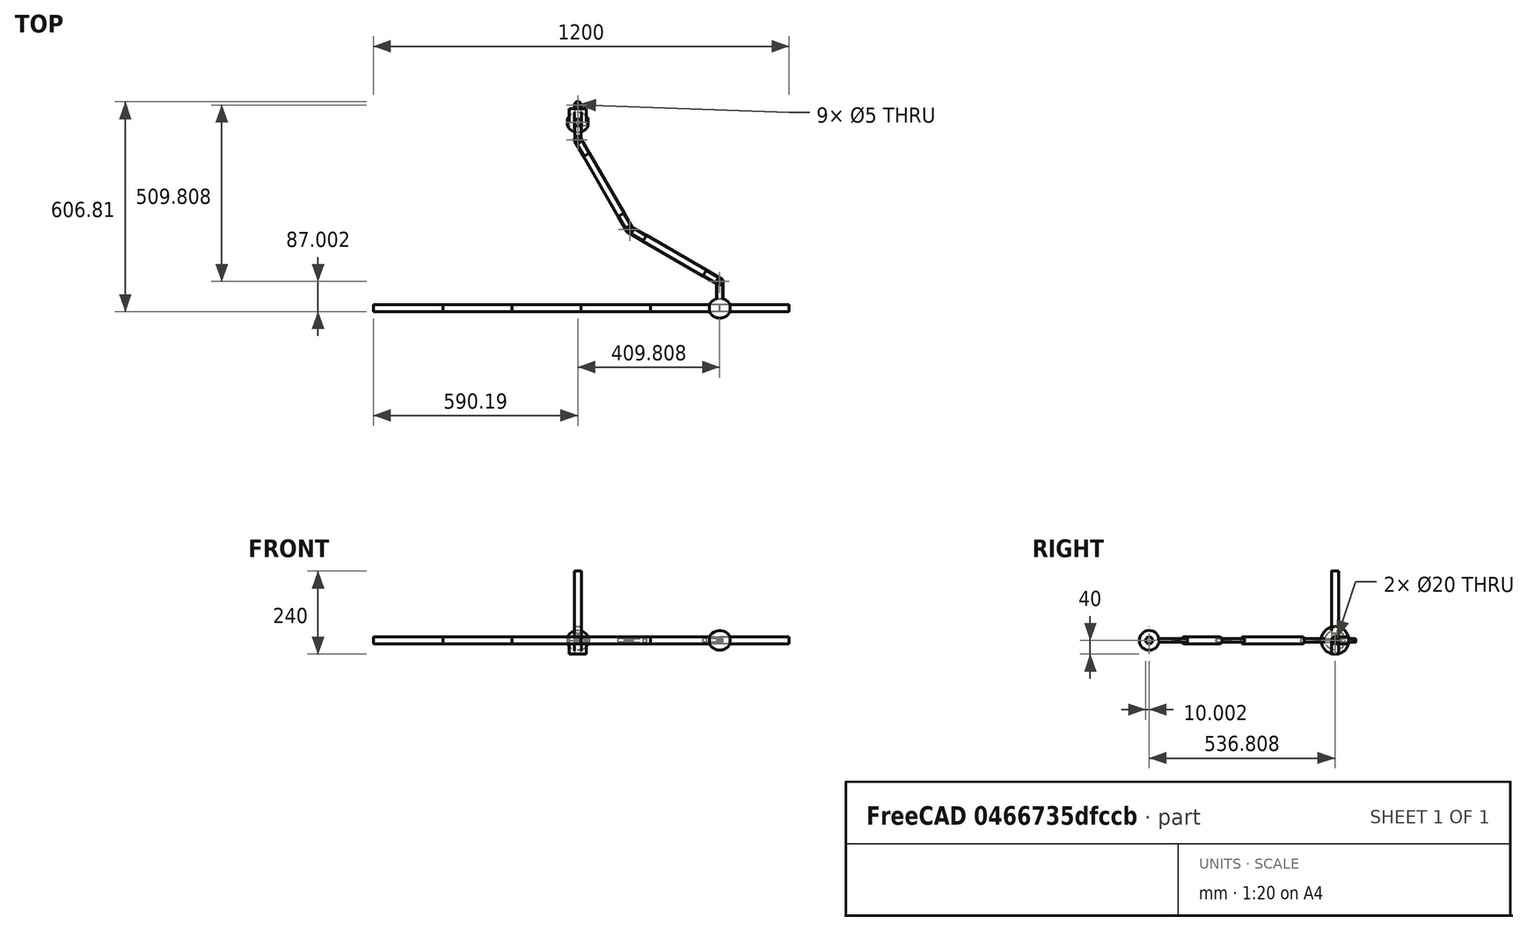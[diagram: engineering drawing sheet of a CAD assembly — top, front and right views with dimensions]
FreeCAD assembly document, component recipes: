
FREECAD ASSEMBLY — COMPONENT RECIPES ("Demo3Rev")

This assembly document has 7 components, labeled P0..P6 below (a component is one placed body or linked part). 7 of them carry a construction recipe — the FreeCAD feature program that regenerates the part from scratch, quoted from this document or its linked companion documents; the rest are supplied as boundary geometry only. No exploded tour is included for this assembly.
COMPONENT P0 — recipe-attached ("Weight", modeled in this document).
Construction recipe (the document's own serialized feature program — sketch geometry with constraints, then the solid features built on it; lengths are millimeters unless a unit is written):

FEATURE [Sketcher::SketchObject] Sketch
  FullyConstrained = true
  MapMode = 5
  Support = -> [XY_Plane]
  sketch-geometry (2):
    g0: LineSegment StartX=-30 StartY=10 StartZ=0 EndX=30 EndY=10 EndZ=0
    g1: ArcOfCircle CenterX=0 CenterY=-5 CenterZ=0 NormalX=0 NormalY=0 NormalZ=1 AngleXU=0 Radius=33.541 StartAngle=0.463648 EndAngle=2.67795
  constraints (7):
    c: Horizontal(g0)
    c: DistanceY(g-1,g0) = 10
    c: DistanceX(g-1,g0) = 30
    c: PointOnObject(g1,g-2)
    c: DistanceY(g1,g-1) = 5
    c: Coincident(g1,g0)
    c: Coincident(g1,g0)
FEATURE [PartDesign::Revolution] Revolution
  Angle = 360
  Axis = (1,0,0)
  Base = (0,0,0)
  Profile = -> Sketch
  ReferenceAxis = -> Sketch [H_Axis]
FEATURE [PartDesign::CoordinateSystem] WeightTop
  AttacherType = Attacher::AttachEngine3D
  MapMode = 11
  Placement = pos=(30,-1.8e-15,0) rot=(0.707107,0,0.707107;3.14159rad)
  Support = -> [Revolution]
FEATURE [PartDesign::CoordinateSystem] WeightBot
  AttacherType = Attacher::AttachEngine3D
  MapMode = 11
  Placement = pos=(-30,0,0) rot=(0.707107,0,0.707107;3.14159rad)
  Support = -> [Revolution]
FEATURE [PartDesign::CoordinateSystem] WeightLCS
  AttacherType = Attacher::AttachEngine3D
  MapMode = 2
  Support = -> [Body003]
FEATURE [PartDesign::Body] Body  label="Weight"
  Group = -> [Sketch,Revolution,WeightLCS,WeightTop,WeightBot]
  Origin = -> Origin
  Tip = -> Revolution
COMPONENT P1 — recipe-attached ("Rod", modeled in this document).
Construction recipe (the document's own serialized feature program — sketch geometry with constraints, then the solid features built on it; lengths are millimeters unless a unit is written):

FEATURE [Sketcher::SketchObject] Sketch001
  FullyConstrained = true
  MapMode = 5
  Support = -> [XY_Plane001]
  sketch-geometry (1):
    g0: Circle CenterX=0 CenterY=0 CenterZ=0 NormalX=0 NormalY=0 NormalZ=1 AngleXU=0 Radius=10
  constraints (2):
    c: Coincident(g0,g-1)
    c: Diameter(g0) = 20
FEATURE [PartDesign::Pad] Pad
  Direction = (0,0,1)
  Length = 200
  Length2 = 10
  Profile = -> Sketch001
  ReferenceAxis = -> Sketch001 [N_Axis]
  Type = 0
FEATURE [PartDesign::CoordinateSystem] RodTop
  AttacherType = Attacher::AttachEngine3D
  MapMode = 11
  Placement = pos=(0,0,200) rot=(0,0,1;1.5708rad)
  Support = -> [Pad]
FEATURE [PartDesign::CoordinateSystem] RodBottom
  AttacherType = Attacher::AttachEngine3D
  MapMode = 11
  Placement = pos=(0,0,0) rot=(0,0,1;1.5708rad)
  Support = -> [Pad]
FEATURE [PartDesign::Body] Body001  label="Rod"
  Group = -> [Sketch001,Pad,RodTop,RodBottom]
  Origin = -> Origin001
  Tip = -> Pad
COMPONENT P2 — recipe-attached ("LugBody", modeled in this document).
Construction recipe (the document's own serialized feature program — sketch geometry with constraints, then the solid features built on it; lengths are millimeters unless a unit is written):

FEATURE [Sketcher::SketchObject] Sketch002
  FullyConstrained = true
  MapMode = 5
  Support = -> [XY_Plane002]
  sketch-geometry (5):
    g0: LineSegment StartX=-10 StartY=0 StartZ=0 EndX=-10 EndY=50 EndZ=0
    g1: ArcOfCircle CenterX=0 CenterY=50 CenterZ=0 NormalX=0 NormalY=0 NormalZ=1 AngleXU=0 Radius=10 StartAngle=1e-16 EndAngle=3.14159
    g2: LineSegment StartX=10 StartY=50 StartZ=0 EndX=10 EndY=0 EndZ=0
    g3: LineSegment StartX=10 StartY=0 StartZ=0 EndX=-10 EndY=0 EndZ=0
    g4: Circle CenterX=0 CenterY=50 CenterZ=0 NormalX=0 NormalY=0 NormalZ=1 AngleXU=0 Radius=2.5
  constraints (13):
    c: PointOnObject(g0,g-1)
    c: Vertical(g0)
    c: Tangent(g0,g1) = 1.5708
    c: Tangent(g1,g2) = 1.5708
    c: Coincident(g2,g3)
    c: Coincident(g3,g0)
    c: Horizontal(g3)
    c: PointOnObject(g1,g-2)
    c: Vertical(g2)
    c: Diameter(g1) = 20
    c: Distance(g2) = 50
    c: Coincident(g4,g1)
    c: Diameter(g4) = 5
FEATURE [PartDesign::Pad] Pad001
  Direction = (0,0,1)
  Length = 10
  Length2 = 10
  Midplane = true
  Profile = -> Sketch002
  ReferenceAxis = -> Sketch002 [N_Axis]
  Type = 0
FEATURE [PartDesign::Body] Body002  label="LugBody"
  Group = -> [Sketch002,Pad001]
  Origin = -> Origin002
  Tip = -> Pad001
COMPONENT P3 — recipe-attached ("LugCylinder", modeled in this document).
Construction recipe (the document's own serialized feature program — sketch geometry with constraints, then the solid features built on it; lengths are millimeters unless a unit is written):

FEATURE [Sketcher::SketchObject] Sketch003
  FullyConstrained = true
  MapMode = 5
  Placement = pos=(0,0,0) rot=(1,0,0;1.5708rad)
  Support = -> [XZ_Plane003]
  sketch-geometry (1):
    g0: Circle CenterX=0 CenterY=0 CenterZ=0 NormalX=0 NormalY=0 NormalZ=1 AngleXU=0 Radius=10
  constraints (2):
    c: Coincident(g0,g-1)
    c: Diameter(g0) = 20
FEATURE [PartDesign::Pad] Pad002
  Direction = (0,-1,-2e-16)
  Length = 60
  Length2 = 10
  Placement = pos=(0,0,0) rot=(1,0,0;1.5708rad)
  Profile = -> Sketch003
  ReferenceAxis = -> Sketch003 [N_Axis]
  Reversed = true
  Type = 0
FEATURE [PartDesign::Boolean] Boolean
  BaseFeature = -> Pad002
  Group = -> [Body002]
  Type = 2
FEATURE [PartDesign::CoordinateSystem] LugHole
  AttacherType = Attacher::AttachEngine3D
  MapMode = 11
  Placement = pos=(0,50,5) rot=(0,0,1;1.5708rad)
  Support = -> [Boolean]
FEATURE [PartDesign::CoordinateSystem] LugFace
  AttacherType = Attacher::AttachEngine3D
  MapMode = 5
  Placement = pos=(0,0,0) rot=(1,0,0;1.5708rad)
  Support = -> [Boolean]
FEATURE [PartDesign::CoordinateSystem] LugRot30
  AttacherType = Attacher::AttachEngine3D
  AttachmentOffset = pos=(0,0,0) rot=(0,0,1;0.523599rad)
  MapMode = 11
  Placement = pos=(0,50,5) rot=(0,0,1;2.0944rad)
  Support = -> [Boolean]
FEATURE [PartDesign::CoordinateSystem] LugRot60
  AttacherType = Attacher::AttachEngine3D
  AttachmentOffset = pos=(0,0,0) rot=(0,0,1;1.0472rad)
  MapMode = 11
  Placement = pos=(0,50,5) rot=(0,0,1;2.61799rad)
  Support = -> [Boolean]
FEATURE [PartDesign::Body] Body003  label="LugCylinder"
  Group = -> [Sketch003,Pad002,Boolean,LugHole,LugFace,LugRot30,LugRot60]
  Origin = -> Origin003
  Tip = -> Boolean
COMPONENT P4 — recipe-attached ("BobBody", modeled in this document).
Construction recipe (the document's own serialized feature program — sketch geometry with constraints, then the solid features built on it; lengths are millimeters unless a unit is written):

FEATURE [Sketcher::SketchObject] Sketch004
  FullyConstrained = true
  MapMode = 5
  Support = -> [XY_Plane004]
  sketch-geometry (4):
    g0: LineSegment StartX=-10 StartY=0 StartZ=0 EndX=-10 EndY=30 EndZ=0
    g1: ArcOfCircle CenterX=0 CenterY=30 CenterZ=0 NormalX=0 NormalY=0 NormalZ=1 AngleXU=0 Radius=10 StartAngle=2e-16 EndAngle=3.14159
    g2: LineSegment StartX=10 StartY=30 StartZ=0 EndX=10 EndY=0 EndZ=0
    g3: LineSegment StartX=10 StartY=0 StartZ=0 EndX=-10 EndY=0 EndZ=0
  constraints (11):
    c: PointOnObject(g0,g-1)
    c: Vertical(g0)
    c: Tangent(g0,g1) = 1.5708
    c: Tangent(g1,g2) = 1.5708
    c: Coincident(g2,g3)
    c: Coincident(g3,g0)
    c: Vertical(g2)
    c: PointOnObject(g1,g-2)
    c: Diameter(g1) = 20
    c: Distance(g0) = 30
    c: PointOnObject(g2,g-1)
FEATURE [PartDesign::Revolution] Revolution001
  Angle = 360
  Axis = (1,0,0)
  Base = (0,0,0)
  Profile = -> Sketch004
  ReferenceAxis = -> Sketch004 [H_Axis]
FEATURE [PartDesign::CoordinateSystem] BobBody  label="BobBody001"
  AttacherType = Attacher::AttachEngine3D
  MapMode = 11
  Placement = pos=(-10,0,0) rot=(0.707107,0,0.707107;3.14159rad)
  Support = -> [Revolution001]
FEATURE [PartDesign::Body] Body004  label="BobBody"
  Group = -> [Sketch004,Revolution001,BobBody]
  Origin = -> Origin004
  Tip = -> Revolution001
COMPONENT P5 — recipe-attached ("GroundBody", modeled in this document).
Construction recipe (the document's own serialized feature program — sketch geometry with constraints, then the solid features built on it; lengths are millimeters unless a unit is written):

FEATURE [Sketcher::SketchObject] Sketch005
  FullyConstrained = true
  MapMode = 5
  Support = -> [XY_Plane005]
  sketch-geometry (4):
    g0: LineSegment StartX=-25 StartY=10 StartZ=0 EndX=25 EndY=10 EndZ=0
    g1: LineSegment StartX=25 StartY=10 StartZ=0 EndX=25 EndY=-10 EndZ=0
    g2: LineSegment StartX=25 StartY=-10 StartZ=0 EndX=-25 EndY=-10 EndZ=0
    g3: LineSegment StartX=-25 StartY=-10 StartZ=0 EndX=-25 EndY=10 EndZ=0
  constraints (11):
    c: Coincident(g0,g1)
    c: Coincident(g1,g2)
    c: Coincident(g2,g3)
    c: Coincident(g3,g0)
    c: Horizontal(g0)
    c: Horizontal(g2)
    c: Vertical(g1)
    c: Vertical(g3)
    c: DistanceY(g2,g0) = 20
    c: DistanceX(g0,g0) = 50
    c: Symmetric(g0,g1,g-1)
FEATURE [PartDesign::Pad] Pad003
  Direction = (0,0,1)
  Length = 40
  Length2 = 10
  Profile = -> Sketch005
  ReferenceAxis = -> Sketch005 [N_Axis]
  Reversed = true
  Type = 0
FEATURE [PartDesign::CoordinateSystem] GroundLCS
  AttacherType = Attacher::AttachEngine3D
  MapMode = 5
  Placement = pos=(0,0,-40) rot=(1,0,0;3.14159rad)
  Support = -> [Pad003]
FEATURE [PartDesign::Body] Body005  label="GroundBody"
  Group = -> [Sketch005,Pad003,GroundLCS]
  Origin = -> Origin005
  Tip = -> Pad003
COMPONENT P6 — recipe-attached ("Spacer", modeled in this document).
Construction recipe (the document's own serialized feature program — sketch geometry with constraints, then the solid features built on it; lengths are millimeters unless a unit is written):

FEATURE [Sketcher::SketchObject] Sketch006
  FullyConstrained = true
  MapMode = 5
  Support = -> [XY_Plane007]
  sketch-geometry (2):
    g0: Circle CenterX=0 CenterY=0 CenterZ=0 NormalX=0 NormalY=0 NormalZ=1 AngleXU=0 Radius=10
    g1: Circle CenterX=0 CenterY=0 CenterZ=0 NormalX=0 NormalY=0 NormalZ=1 AngleXU=0 Radius=2.5
  constraints (4):
    c: Coincident(g0,g-1)
    c: Coincident(g1,g0)
    c: Diameter(g0) = 20
    c: Diameter(g1) = 5
FEATURE [PartDesign::Pad] Pad004
  Direction = (0,0,1)
  Length = 20
  Length2 = 10
  Profile = -> Sketch006
  ReferenceAxis = -> Sketch006 [N_Axis]
  Type = 0
FEATURE [PartDesign::CoordinateSystem] SpacerTop
  AttacherType = Attacher::AttachEngine3D
  MapMode = 11
  Placement = pos=(0,0,20) rot=(0,0,1;1.5708rad)
  Support = -> [Pad004]
FEATURE [PartDesign::Body] Body006  label="Spacer"
  Group = -> [Sketch006,Pad004,SpacerTop]
  Origin = -> Origin007
  Tip = -> Pad004
PROVENANCE & LICENSES
A FreeCAD (.FCStd) document from a public repository crawl; recipes are the document's own serialized feature recipes (and, for linked parts, companion documents' recipes).
License: gpl-3.0.
